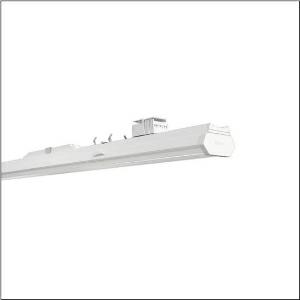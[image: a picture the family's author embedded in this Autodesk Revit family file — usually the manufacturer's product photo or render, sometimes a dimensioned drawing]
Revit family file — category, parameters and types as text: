
# Revit family: licross_21_protected_mo_52td12dn48xg
name_source: partatom
category: Lighting Fixtures
units: mm (PartAtom-declared; Revit-internal decimal feet)

## family parameters
Cut with Voids When Loaded = No
Host = Face
Light Source = No
Part Type = Normal
Room Calculation Point = No
Round Connector Dimension = Use Diameter
Shared = No

## types (1)
- --- (1 x LED, 8000 lm, 45.3 W, 4000K)
    Apparent Load = 45 VA
    CIE Flux Codes = 73 92 98 99 100
    Color Rendering = 80
    Color Temperature = 4000K
    Default Elevation = 1800 mm
    Description = Licross 21 Protected MO, luminaire insert, of sheet steel, galvanised, coil coated, white, length: 1.500mm, width: 90mm, height: 103mm, LED rated luminous flux: 8.000lm, light colour: 840, SDCM (Standard Deviation of Colour Matching)MacAdam ≤ 3 SDCM (initial), control gear: DALI 2, with plug, 5-pole, with phase selection, mains connection: 220..240V, AC, 50/60Hz, rated input power: 45W, internal wiring halogen-free, primary light control with lens, of plastic, primary optical cover: cover, of PMMA, light emission: direct distribution, primary light characteristic: symmetric, protection rating (complete): IP54, insulation class (complete): insulation class I (protective earthing), certification: CE, ENEC, VDE, UKCA, protection symbol: D if used in an environment with non-conductive dust loads with corresponding accessories, impact resistance: IK06, permissible ambient temperature for indoor applications: -25..+45°C, corresponds to IFS (International Featured Standards) requirements for safety and quality in the food industry, reducing of maximum allowable ambient temperature of 5°C with ceiling mounting, LABS conformity tested according to VDMA 24364:2018-05, The light source and the operating device comply with the requirements of the Ecodesign Regulation (EU) 2019/2020 and are replaceable in accordance with this regulation, packaging unit: 1 piece
    Height = 92 mm
    Lamp = 1 x LED
    Lamp Light Flux = 8000 lm
    Lamp Power = 45.3 W
    Lamp count = 1
    Length = 1500 mm
    Luminous efficacy = 177 lm/W
    Manufacturer = Siteco
    ModVariant = No
    Model = 52TD12DN48XG
    Mounting Place = Ceiling
    Mounting Type = Pendant
    Number of Poles = 1
    OnlyDefault = Yes
    Power Factor = 1
    Product Name = Licross 21 Protected MO
    Product group = luminaire insert | ceiling pendant
    ProductGroupID = 901
    Protection Class = Protection class I
    Protection Degree = IP 54
    RLX_Detail_Level = 1
    RLX_Emergency_Light_Flux = 0 lm
    RLX_Emergency_Type = 0
    RLX_Emergency_Type_DB = No
    RlxData = <blob elided: 24733 chars, md5=0cc2cf6e>
    Socket = socket
    Standby Power = 0 W
    System Light Flux = 8000 lm
    System Power = 45 W
    Type Comments = factory setting: luminous flux: 100 % | dim-lin: 254 | 305 mA
    Type Image = l_1256148.jpg
    URL = http://relux.com
    VarID = @adj_128887
    Voltage = 0 V
    Weight = 0.00 kg
    Width = 88 mm

## geometry (parser evidence)
native form markers: Blend x4, Sweep x9
no freeform markers — native parametric forms only
